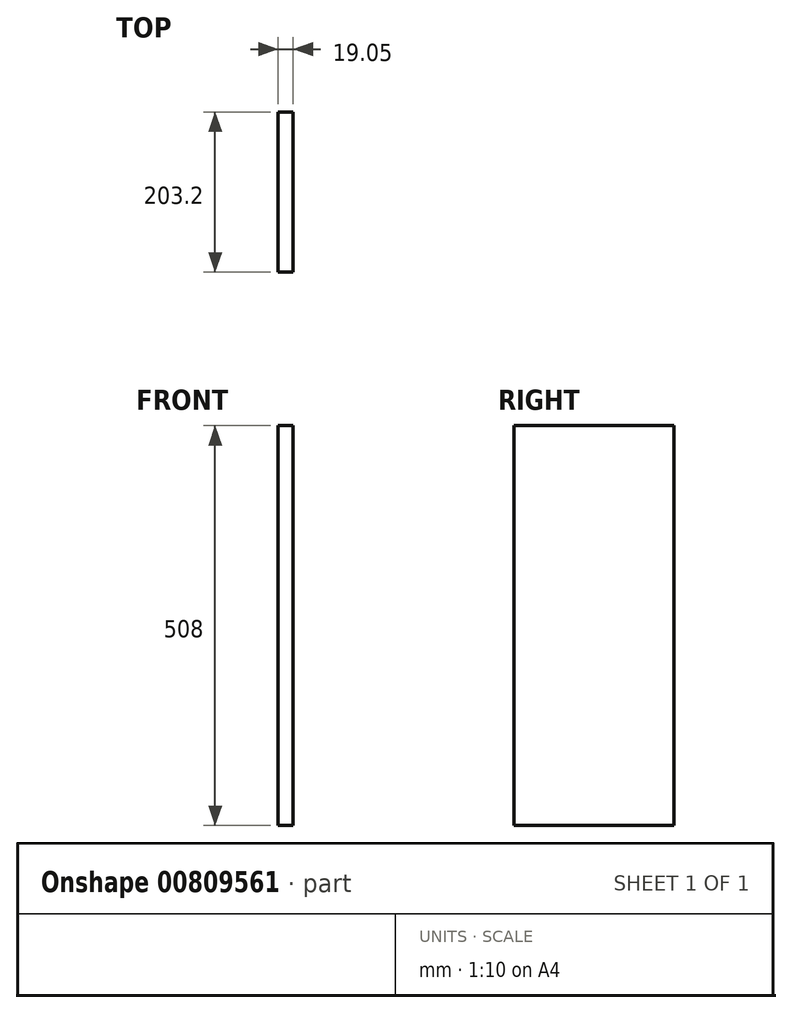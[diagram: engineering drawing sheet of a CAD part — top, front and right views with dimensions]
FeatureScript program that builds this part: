
annotation { "Feature Type Name" : "Feature", "Feature Type Description" : "" }
export const myFeature = defineFeature(function(context is Context, id is Id, definition is map)
    precondition{}
    {
        {
            var Q0;
            Q0=qCreatedBy(makeId("Right.planeOp"),FACE);
            var sketch = newSketch(context, id + "F0", { "sketchPlane" : qUnion([Q0])});
            skLineSegment(sketch, "E0.bottom", {"start": v(101.6, -254) * mm, "end": v(-101.6, -254) * mm});
            skLineSegment(sketch, "E0.top", {"start": v(101.6, 254) * mm, "end": v(-101.6, 254) * mm});
            skLineSegment(sketch, "E0.left", {"start": v(101.6, -254) * mm, "end": v(101.6, 254) * mm});
            skLineSegment(sketch, "E0.right", {"start": v(-101.6, -254) * mm, "end": v(-101.6, 254) * mm});
            skPoint(sketch, "E0.middle", {"position": v(0, 0) * mm});
            skSolve(sketch);
        }
        {
            var Q0;
            Q0=makeQuery(id+"F0.imprint","IMPRINT",FACE,{"disambiguationData":[TD([[makeQuery(id+"F0.imprint","IMPRINT",EDGE,{"derivedFrom":sQuery(id+"F0.wireOp",EDGE,"E0.bottom")}),-1.0]])]});
            extrude(context, id + "F1", {"entities" : qUnion([Q0]), "depth" : 19.05 * mm, "offsetDistance" : 25.4 * mm});
        }
    });
